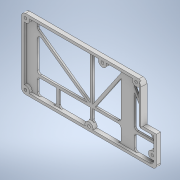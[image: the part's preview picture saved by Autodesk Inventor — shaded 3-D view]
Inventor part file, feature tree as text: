
AUTODESK INVENTOR PART (.ipt)
format: ipt  version: 2021 (Build 250183000, 183)  size: 503,808 bytes
history: native  units: mm
features: sketch x16, extrude x15, fillet x7, hole x1
ambient origin geometry x8: Origin, YZ Plane, XZ Plane, XY Plane, X Axis, Y Axis, Z Axis, Center Point
bodies: Solid1 (feature_tree)
feature tree (39):
  extrude  "Extrusion1"  Depth=52.0mm
  fillet  "Fillet1"  Radius=2.0mm
  extrude  "Extrusion2"  Depth=2.0mm
  hole  "Hole1"  [1 undecoded]
  extrude  "Extrusion3"  Depth=3.0mm
  extrude  "Extrusion4"  Depth=3.0mm
  fillet  "Fillet2"  Radius=50.0mm
  fillet  "Fillet3"  Radius=8.0mm
  extrude  "Extrusion5"  Depth=3.0mm
  extrude  "Extrusion6"  Depth=49.0mm
  fillet  "Fillet4"  Radius=49.0mm
  extrude  "Extrusion7"  Depth=49.0mm
  extrude  "Extrusion8"  Depth=6.0mm
  extrude  "Extrusion9"  Depth=6.0mm
  fillet  "Fillet5"  Radius=6.0mm
  extrude  "Extrusion10"  Depth=24.0mm
  extrude  "Extrusion11"  Depth=2.0mm
  extrude  "Extrusion12"  Depth=2.0mm
  fillet  "Fillet6"  Radius=2.0mm
  fillet  "Fillet7"  Radius=2.0mm
  extrude  "Extrusion13"  Depth=2.0mm
  extrude  "Extrusion14"  Depth=1.2mm TaperAngle=0.0deg
  extrude  "Extrusion15"  Depth=25.0mm
  sketch  "Sketch1"  dims[d0=100.0mm d1=52.0mm d2=2.0mm]
  sketch  "Sketch2"  dims[d3=2.0mm d4=2.0mm]
  sketch  "Sketch3"  dims[d5=2.0mm d6=3.0mm d7=0.0mm]
  sketch  "Sketch4"  dims[d8=3.0mm d9=3.0mm]
  sketch  "Sketch5"  dims[d10=3.0mm d11=3.0mm d12=50.0mm d13=8.0mm]
  sketch  "Sketch6"  dims[d14=97.0mm d15=3.0mm]
  sketch  "Sketch7"  dims[d16=49.0mm d17=60.0mm d18=49.0mm]
  sketch  "Sketch8"  dims[d19=85.0mm d20=49.0mm]
  sketch  "Sketch9"  dims[d21=6.0mm d22=6.0mm]
  sketch  "Sketch10"  dims[d23=6.0mm d24=6.0mm d25=6.0mm]
  sketch  "Sketch11"  dims[d26=3.0mm d27=0.0mm]
  sketch  "Sketch12"  dims[d28=2.0mm d29=6.0mm d30=4.0mm d31=2.0mm d32=90.0deg d33=4.0mm d34=20.594885mm d35=24.0mm]
  sketch  "Sketch13"  dims[d36=2.0mm d37=2.0mm]
  sketch  "Sketch14"  dims[d38=15.0mm d39=15.0mm d40=2.0mm d41=2.0mm]
  sketch  "Sketch15"  dims[d42=2.0mm d43=2.0mm]
  sketch  "Sketch16"  dims[d44=2.0mm d45=1.2mm d46=0.0mm d47=25.0mm d48=2.0mm d49=1.2mm d50=0.0mm d51=2.0mm d52=2.0mm d53=12.0mm d54=29.0mm d55=10.0mm d56=0.0mm d57=2.0mm d58=2.0mm d59=3.0mm d60=0.0mm d61=3.0mm d62=1.4mm d63=1.4mm d64=3.0mm d65=1.5mm d66=0.0mm d67=3.0mm d68=1.0mm d69=1.0mm d70=3.0mm d71=2.0mm d72=0.0mm d73=3.0mm d74=1.5mm d75=0.0mm d76=3.0mm d77=1.5mm d78=0.0mm d79=10.0mm d80=18.0mm d81=1.0mm d82=1.0mm d83=3.0mm d84=1.2mm d85=0.0mm d86=41.096396mm d87=10.0mm d88=5.0mm d89=5.0mm d90=3.0mm d91=0.8mm d92=4.5mm d93=1.2mm d94=0.0mm d95=2.0mm d96=2.0mm d97=5.0mm d98=0.0mm d99=2.0mm d100=3.0mm d101=0.0mm d102=0.2mm d103=1.5mm d104=0.0mm]
note: 1 required parameter value undecoded (feature->parameter linkage not recoverable at this tier; creation-order binding heuristic only, values carry confidence <= 0.55)
